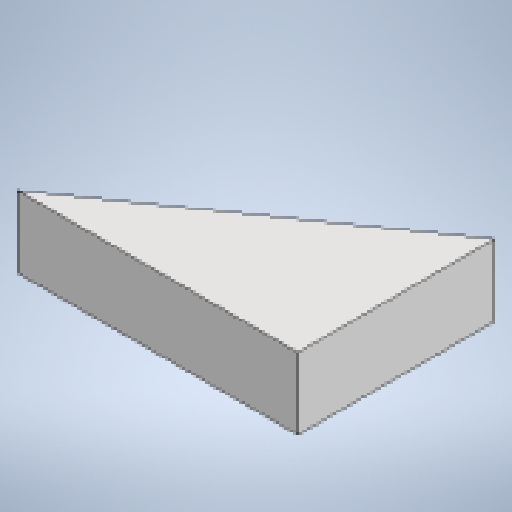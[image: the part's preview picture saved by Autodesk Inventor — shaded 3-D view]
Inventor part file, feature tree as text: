
AUTODESK INVENTOR PART (.ipt)
format: ipt  version: 2025 (Build 290162010, 162A)  size: 124,416 bytes
history: native  units: mm
features: extrude x1, sketch x1
ambient origin geometry x8: Origin, YZ Plane, XZ Plane, XY Plane, X Axis, Y Axis, Z Axis, Center Point
bodies: Solid1 (feature_tree)
feature tree (2):
  extrude  "Extrusion1"  Depth=800.0mm
  sketch  "Sketch1"  dims[d0=2200.0mm d1=6.108652mm d2=800.0mm d3=0.0mm]
